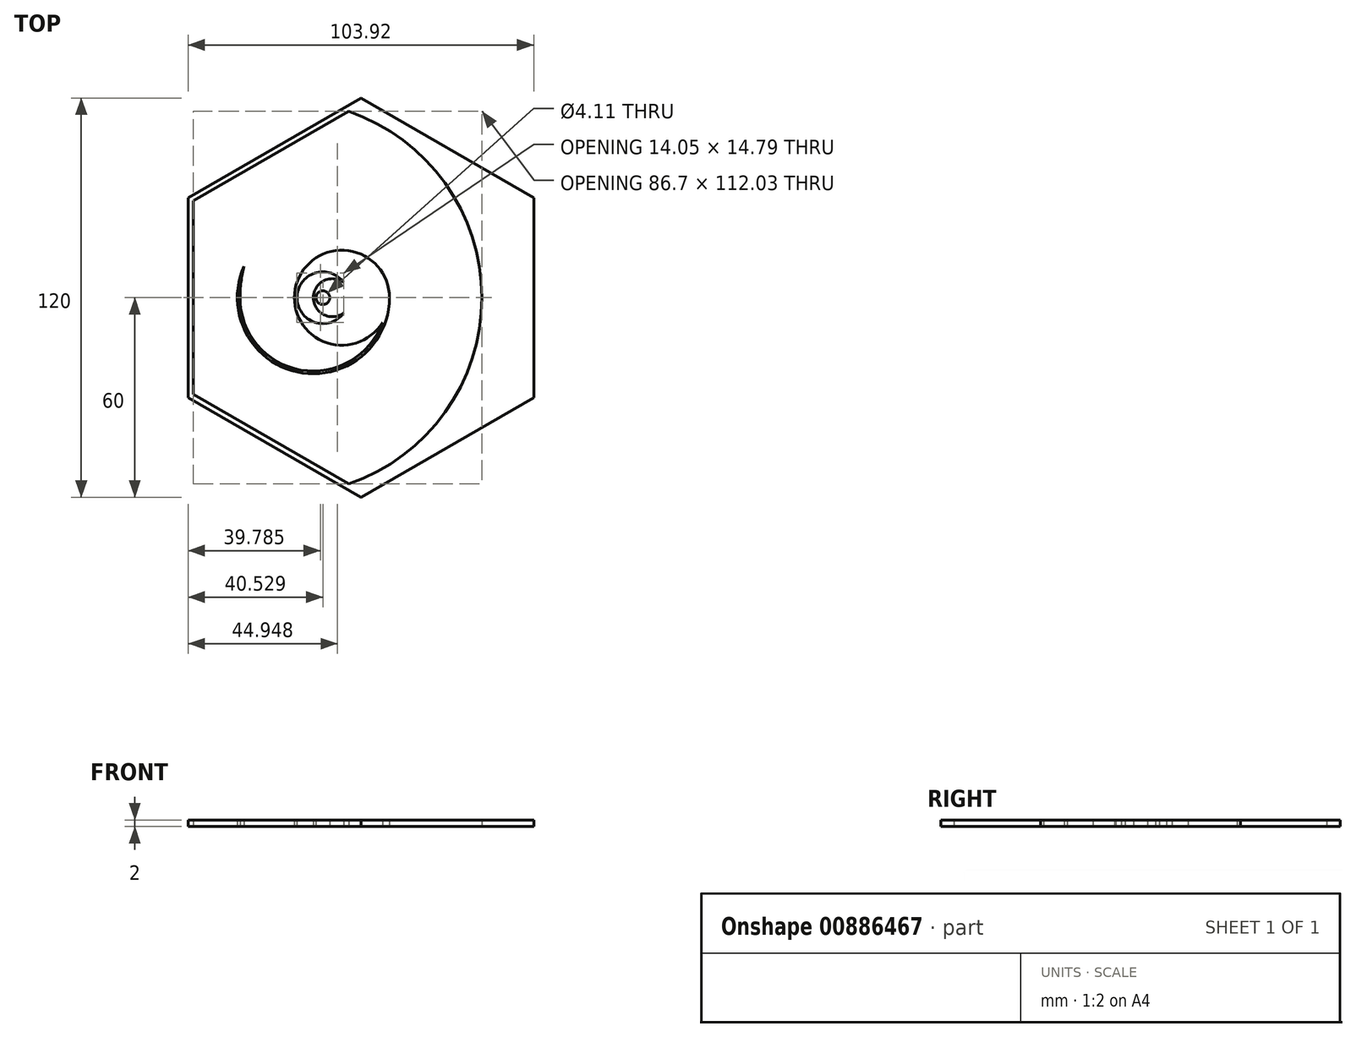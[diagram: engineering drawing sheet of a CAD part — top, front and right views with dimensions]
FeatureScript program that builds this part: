
annotation { "Feature Type Name" : "Feature", "Feature Type Description" : "" }
export const myFeature = defineFeature(function(context is Context, id is Id, definition is map)
    precondition{}
    {
        {
            var Q0;
            Q0=qCreatedBy(makeId("Top.planeOp"),FACE);
            var sketch = newSketch(context, id + "F0", { "sketchPlane" : qUnion([Q0])});
            skArc(sketch, "E0", {"start": v(41.43, 32.17) * mm, "mid": v(-14.29, 0) * mm, "end": v(41.43, -32.17) * mm});
            skCircle(sketch, "E1", {"center": v(8.57, 0) * mm, "radius": 22.86 * mm});
            skCircle(sketch, "E2", {"center": v(17.14, 0) * mm, "radius": 14.29 * mm});
            skCircle(sketch, "E3", {"center": v(11.43, 0) * mm, "radius": 8.57 * mm});
            skCircle(sketch, "E4", {"center": v(14.29, 0) * mm, "radius": 5.71 * mm});
            skArc(sketch, "E5.0", {"start": v(42.26, 30.73) * mm, "mid": v(-13.49, 0) * mm, "end": v(42.26, -30.73) * mm});
            skCircle(sketch, "E6.0", {"center": v(8.57, 0) * mm, "radius": 22.06 * mm});
            skCircle(sketch, "E7.0", {"center": v(17.14, 0) * mm, "radius": 13.49 * mm});
            skCircle(sketch, "E8.0", {"center": v(11.43, 0) * mm, "radius": 7.77 * mm});
            skCircle(sketch, "E9.0", {"center": v(14.29, 0) * mm, "radius": 4.91 * mm});
            skArc(sketch, "E10.trimOffspring", {"start": v(59.17, -1.43) * mm, "mid": v(59.2, 0) * mm, "end": v(59.17, 1.43) * mm});
            skCircle(sketch, "E11", {"center": v(22.86, 0) * mm, "radius": 36.34 * mm});
            skCircle(sketch, "E12", {"center": v(22.86, 0) * mm, "radius": 37.14 * mm});
            skCircle(sketch, "E13", {"center": v(11.43, 0) * mm, "radius": 2.86 * mm});
            skCircle(sketch, "E14.0", {"center": v(11.43, 0) * mm, "radius": 2.06 * mm});
            skCircle(sketch, "E15.cCircle", {"center": v(22.86, 0) * mm, "radius": 60 * mm, "construction": true});
            skLineSegment(sketch, "E15.0", {"start": v(-29.1, 30) * mm, "end": v(22.86, 60) * mm});
            skLineSegment(sketch, "E15.1", {"start": v(22.86, 60) * mm, "end": v(74.82, 30) * mm});
            skLineSegment(sketch, "E15.2", {"start": v(74.82, 30) * mm, "end": v(74.82, -30) * mm});
            skLineSegment(sketch, "E15.3", {"start": v(74.82, -30) * mm, "end": v(22.86, -60) * mm});
            skLineSegment(sketch, "E15.4", {"start": v(22.86, -60) * mm, "end": v(-29.1, -30) * mm});
            skLineSegment(sketch, "E15.5", {"start": v(-29.1, -30) * mm, "end": v(-29.1, 30) * mm});
            skArc(sketch, "E16", {"start": v(18.05, -57.22) * mm, "mid": v(60, 0) * mm, "end": v(18.05, 57.22) * mm});
            skArc(sketch, "E17.0", {"start": v(17.1, -56.68) * mm, "mid": v(59.2, 0) * mm, "end": v(17.1, 56.68) * mm});
            skLineSegment(sketch, "E18.0", {"start": v(-27.5, -29.08) * mm, "end": v(-27.5, 29.08) * mm});
            skLineSegment(sketch, "E18.1", {"start": v(22.86, 58.15) * mm, "end": v(73.22, 29.08) * mm});
            skLineSegment(sketch, "E18.2", {"start": v(73.22, 29.08) * mm, "end": v(73.22, -29.08) * mm});
            skLineSegment(sketch, "E18.3", {"start": v(-27.5, 29.08) * mm, "end": v(22.86, 58.15) * mm});
            skLineSegment(sketch, "E18.4", {"start": v(73.22, -29.08) * mm, "end": v(22.86, -58.15) * mm});
            skLineSegment(sketch, "E18.5", {"start": v(22.86, -58.15) * mm, "end": v(-27.5, -29.08) * mm});
            skPoint(sketch, "E19.orphan", {"position": v(-70.83, -30.73) * mm});
            skPoint(sketch, "E20.MirrorCS.start.orphan", {"position": v(-70.83, 30.73) * mm});
            skPoint(sketch, "E21.orphan", {"position": v(-70.03, -30.73) * mm});
            skPoint(sketch, "E22.orphan", {"position": v(-70.03, 30.73) * mm});
            skSolve(sketch);
        }
        {
            var Q0;
            {var subQ11=sQuery(id+"F0.wireOp",EDGE,"E15.1");Q0=makeQuery(id+"F0.imprint","IMPRINT",FACE,{"disambiguationData":[TD([[makeQuery(id+"F0.imprint","IMPRINT",EDGE,{"derivedFrom":subQ11}),-1.0]])]});}
            var Q1;
            {var subQ5=sQuery(id+"F0.wireOp",EDGE,"E15.5");Q1=makeQuery(id+"F0.imprint","IMPRINT",FACE,{"disambiguationData":[TD([[makeQuery(id+"F0.imprint","IMPRINT",EDGE,{"derivedFrom":subQ5}),-1.0]])]});}
            var Q2;
            {var subQ0=sQuery(id+"F0.wireOp",EDGE,"E16");var subQ1=sQuery(id+"F0.wireOp",EDGE,"E15.0");var subQ2=makeQuery(id+"F0.imprint","INTERSECT",VERTEX,{"derivedFrom":[subQ1,subQ0]});Q2=makeQuery(id+"F0.imprint","IMPRINT",FACE,{"disambiguationData":[TD([[makeQuery(id+"F0.imprint","IMPRINT",EDGE,{"disambiguationData":[TD([[subQ2,1.0]])],"derivedFrom":subQ1}),-1.0]])]});}
            var Q3;
            {var subQ0=sQuery(id+"F0.wireOp",EDGE,"E17.0");var subQ1=sQuery(id+"F0.wireOp",EDGE,"E12");var subQ2=makeQuery(id+"F0.imprint","INTERSECT",VERTEX,{"disambiguationData":[OD(0.0)],"derivedFrom":[subQ1,subQ0]});Q3=makeQuery(id+"F0.imprint","IMPRINT",FACE,{"disambiguationData":[TD([[makeQuery(id+"F0.imprint","IMPRINT",EDGE,{"disambiguationData":[TD([[subQ2,1.0]])],"derivedFrom":subQ1}),-1.0]])]});}
            var Q4;
            {var subQ6=sQuery(id+"F0.wireOp",EDGE,"E18.1");Q4=makeQuery(id+"F0.imprint","IMPRINT",FACE,{"disambiguationData":[TD([[makeQuery(id+"F0.imprint","IMPRINT",EDGE,{"derivedFrom":subQ6}),-1.0]])]});}
            var Q5;
            {var subQ0=sQuery(id+"F0.wireOp",EDGE,"E17.0");var subQ1=sQuery(id+"F0.wireOp",EDGE,"E12");var subQ2=makeQuery(id+"F0.imprint","INTERSECT",VERTEX,{"disambiguationData":[OD(0.0)],"derivedFrom":[subQ1,subQ0]});Q5=makeQuery(id+"F0.imprint","IMPRINT",FACE,{"disambiguationData":[TD([[makeQuery(id+"F0.imprint","IMPRINT",EDGE,{"disambiguationData":[TD([[subQ2,1.0]])],"derivedFrom":subQ1}),1.0]])]});}
            var Q6;
            {var subQ0=sQuery(id+"F0.wireOp",EDGE,"E11");var subQ1=makeQuery(id+"F0.imprint","IMPRINT",VERTEX,{"disambiguationData":[OD(0.0)],"derivedFrom":subQ0});Q6=makeQuery(id+"F0.imprint","IMPRINT",FACE,{"disambiguationData":[TD([[makeQuery(id+"F0.imprint","IMPRINT",EDGE,{"disambiguationData":[TD([[subQ1,-1.0]])],"derivedFrom":subQ0}),1.0]])]});}
            var Q7;
            {var subQ0=sQuery(id+"F0.wireOp",EDGE,"E11");var subQ9=makeQuery(id+"F0.imprint","IMPRINT",VERTEX,{"disambiguationData":[OD(0.0)],"derivedFrom":subQ0});Q7=makeQuery(id+"F0.imprint","IMPRINT",FACE,{"disambiguationData":[TD([[makeQuery(id+"F0.imprint","IMPRINT",EDGE,{"disambiguationData":[TD([[subQ9,-1.0]])],"derivedFrom":subQ0}),-1.0]])]});}
            var Q8;
            {var subQ0=sQuery(id+"F0.wireOp",EDGE,"E11");var subQ4=makeQuery(id+"F0.imprint","IMPRINT",VERTEX,{"disambiguationData":[OD(2.0)],"derivedFrom":subQ0});Q8=makeQuery(id+"F0.imprint","IMPRINT",FACE,{"disambiguationData":[TD([[makeQuery(id+"F0.imprint","IMPRINT",EDGE,{"disambiguationData":[TD([[subQ4,-1.0]])],"derivedFrom":subQ0}),-1.0]])]});}
            var Q9;
            {var subQ0=sQuery(id+"F0.wireOp",EDGE,"E16");var subQ1=sQuery(id+"F0.wireOp",EDGE,"E12");var subQ2=makeQuery(id+"F0.imprint","INTERSECT",VERTEX,{"derivedFrom":[subQ1,subQ0]});Q9=makeQuery(id+"F0.imprint","IMPRINT",FACE,{"disambiguationData":[TD([[makeQuery(id+"F0.imprint","IMPRINT",EDGE,{"disambiguationData":[TD([[subQ2,1.0]])],"derivedFrom":subQ1}),-1.0]])]});}
            var Q10;
            {var subQ0=sQuery(id+"F0.wireOp",EDGE,"E16");var subQ1=sQuery(id+"F0.wireOp",EDGE,"E15.4");var subQ2=makeQuery(id+"F0.imprint","INTERSECT",VERTEX,{"derivedFrom":[subQ1,subQ0]});Q10=makeQuery(id+"F0.imprint","IMPRINT",FACE,{"disambiguationData":[TD([[makeQuery(id+"F0.imprint","IMPRINT",EDGE,{"disambiguationData":[TD([[subQ2,-1.0]])],"derivedFrom":subQ1}),-1.0]])]});}
            var Q11;
            {var subQ0=sQuery(id+"F0.wireOp",EDGE,"E2");var subQ1=makeQuery(id+"F0.imprint","INTERSECT",VERTEX,{"derivedFrom":[sQuery(id+"F0.wireOp",EDGE,"E1"),subQ0]});Q11=makeQuery(id+"F0.imprint","IMPRINT",FACE,{"disambiguationData":[TD([[makeQuery(id+"F0.imprint","IMPRINT",EDGE,{"disambiguationData":[TD([[subQ1,-1.0]])],"derivedFrom":subQ0}),1.0]])]});}
            var Q12;
            {var subQ0=sQuery(id+"F0.wireOp",EDGE,"E2");var subQ1=sQuery(id+"F0.wireOp",EDGE,"E1");var subQ2=makeQuery(id+"F0.imprint","INTERSECT",VERTEX,{"derivedFrom":[subQ1,subQ0]});Q12=makeQuery(id+"F0.imprint","IMPRINT",FACE,{"disambiguationData":[TD([[makeQuery(id+"F0.imprint","IMPRINT",EDGE,{"disambiguationData":[TD([[subQ2,1.0]])],"derivedFrom":subQ1}),1.0]])]});}
            var Q13;
            {var subQ0=sQuery(id+"F0.wireOp",EDGE,"E11");var subQ1=sQuery(id+"F0.wireOp",EDGE,"E1");var subQ2=makeQuery(id+"F0.imprint","INTERSECT",VERTEX,{"disambiguationData":[OD(0.0)],"derivedFrom":[subQ1,subQ0]});Q13=makeQuery(id+"F0.imprint","IMPRINT",FACE,{"disambiguationData":[TD([[makeQuery(id+"F0.imprint","IMPRINT",EDGE,{"disambiguationData":[TD([[subQ2,1.0]])],"derivedFrom":subQ1}),1.0]])]});}
            var Q14;
            {var subQ0=sQuery(id+"F0.wireOp",EDGE,"E6.0");var subQ1=sQuery(id+"F0.wireOp",EDGE,"E2");var subQ2=makeQuery(id+"F0.imprint","INTERSECT",VERTEX,{"disambiguationData":[OD(0.0)],"derivedFrom":[subQ1,subQ0]});Q14=makeQuery(id+"F0.imprint","IMPRINT",FACE,{"disambiguationData":[TD([[makeQuery(id+"F0.imprint","IMPRINT",EDGE,{"disambiguationData":[TD([[subQ2,-1.0]])],"derivedFrom":subQ1}),1.0]])]});}
            var Q15;
            {var subQ0=sQuery(id+"F0.wireOp",EDGE,"E3");var subQ1=sQuery(id+"F0.wireOp",EDGE,"E2");var subQ2=makeQuery(id+"F0.imprint","INTERSECT",VERTEX,{"derivedFrom":[subQ1,subQ0]});Q15=makeQuery(id+"F0.imprint","IMPRINT",FACE,{"disambiguationData":[TD([[makeQuery(id+"F0.imprint","IMPRINT",EDGE,{"disambiguationData":[TD([[subQ2,-1.0]])],"derivedFrom":subQ1}),1.0]])]});}
            var Q16;
            {var subQ0=sQuery(id+"F0.wireOp",EDGE,"E4");var subQ1=makeQuery(id+"F0.imprint","INTERSECT",VERTEX,{"derivedFrom":[sQuery(id+"F0.wireOp",EDGE,"E3"),subQ0]});Q16=makeQuery(id+"F0.imprint","IMPRINT",FACE,{"disambiguationData":[TD([[makeQuery(id+"F0.imprint","IMPRINT",EDGE,{"disambiguationData":[TD([[subQ1,-1.0]])],"derivedFrom":subQ0}),1.0]])]});}
            var Q17;
            {var subQ0=sQuery(id+"F0.wireOp",EDGE,"E7.0");var subQ1=sQuery(id+"F0.wireOp",EDGE,"E3");var subQ2=makeQuery(id+"F0.imprint","INTERSECT",VERTEX,{"disambiguationData":[OD(0.0)],"derivedFrom":[subQ1,subQ0]});Q17=makeQuery(id+"F0.imprint","IMPRINT",FACE,{"disambiguationData":[TD([[makeQuery(id+"F0.imprint","IMPRINT",EDGE,{"disambiguationData":[TD([[subQ2,1.0]])],"derivedFrom":subQ1}),1.0]])]});}
            var Q18;
            {var subQ0=sQuery(id+"F0.wireOp",EDGE,"E4");var subQ1=sQuery(id+"F0.wireOp",EDGE,"E3");var subQ2=makeQuery(id+"F0.imprint","INTERSECT",VERTEX,{"derivedFrom":[subQ1,subQ0]});Q18=makeQuery(id+"F0.imprint","IMPRINT",FACE,{"disambiguationData":[TD([[makeQuery(id+"F0.imprint","IMPRINT",EDGE,{"disambiguationData":[TD([[subQ2,1.0]])],"derivedFrom":subQ1}),1.0]])]});}
            var Q19;
            {var subQ0=sQuery(id+"F0.wireOp",EDGE,"E13");var subQ1=sQuery(id+"F0.wireOp",EDGE,"E4");var subQ2=makeQuery(id+"F0.imprint","INTERSECT",VERTEX,{"derivedFrom":[subQ1,subQ0]});Q19=makeQuery(id+"F0.imprint","IMPRINT",FACE,{"disambiguationData":[TD([[makeQuery(id+"F0.imprint","IMPRINT",EDGE,{"disambiguationData":[TD([[subQ2,-1.0]])],"derivedFrom":subQ1}),1.0]])]});}
            var Q20;
            {var subQ0=sQuery(id+"F0.wireOp",EDGE,"E8.0");var subQ1=sQuery(id+"F0.wireOp",EDGE,"E4");var subQ2=makeQuery(id+"F0.imprint","INTERSECT",VERTEX,{"disambiguationData":[OD(0.0)],"derivedFrom":[subQ1,subQ0]});Q20=makeQuery(id+"F0.imprint","IMPRINT",FACE,{"disambiguationData":[TD([[makeQuery(id+"F0.imprint","IMPRINT",EDGE,{"disambiguationData":[TD([[subQ2,-1.0]])],"derivedFrom":subQ1}),1.0]])]});}
            var Q21;
            {var subQ0=sQuery(id+"F0.wireOp",EDGE,"E9.0");var subQ1=makeQuery(id+"F0.imprint","INTERSECT",VERTEX,{"derivedFrom":[subQ0,sQuery(id+"F0.wireOp",EDGE,"E14.0")]});Q21=makeQuery(id+"F0.imprint","IMPRINT",FACE,{"disambiguationData":[TD([[makeQuery(id+"F0.imprint","IMPRINT",EDGE,{"disambiguationData":[TD([[subQ1,1.0]])],"derivedFrom":subQ0}),-1.0]])]});}
            var Q22;
            {var subQ0=sQuery(id+"F0.wireOp",EDGE,"E3");var subQ1=makeQuery(id+"F0.imprint","INTERSECT",VERTEX,{"derivedFrom":[sQuery(id+"F0.wireOp",EDGE,"E2"),subQ0]});Q22=makeQuery(id+"F0.imprint","IMPRINT",FACE,{"disambiguationData":[TD([[makeQuery(id+"F0.imprint","IMPRINT",EDGE,{"disambiguationData":[TD([[subQ1,1.0]])],"derivedFrom":subQ0}),1.0]])]});}
            var Q23;
            {var subQ0=sQuery(id+"F0.wireOp",EDGE,"E7.0");var subQ1=sQuery(id+"F0.wireOp",EDGE,"E3");var subQ2=makeQuery(id+"F0.imprint","INTERSECT",VERTEX,{"disambiguationData":[OD(0.0)],"derivedFrom":[subQ1,subQ0]});Q23=makeQuery(id+"F0.imprint","IMPRINT",FACE,{"disambiguationData":[TD([[makeQuery(id+"F0.imprint","IMPRINT",EDGE,{"disambiguationData":[TD([[subQ2,1.0]])],"derivedFrom":subQ1}),-1.0]])]});}
            var Q24;
            {var subQ0=sQuery(id+"F0.wireOp",EDGE,"E9.0");var subQ1=makeQuery(id+"F0.imprint","INTERSECT",VERTEX,{"derivedFrom":[sQuery(id+"F0.wireOp",EDGE,"E8.0"),subQ0]});Q24=makeQuery(id+"F0.imprint","IMPRINT",FACE,{"disambiguationData":[TD([[makeQuery(id+"F0.imprint","IMPRINT",EDGE,{"disambiguationData":[TD([[subQ1,-1.0]])],"derivedFrom":subQ0}),1.0]])]});}
            var Q25;
            {var subQ0=sQuery(id+"F0.wireOp",EDGE,"E14.0");Q25=makeQuery(id+"F0.imprint","IMPRINT",FACE,{"disambiguationData":[TD([[makeQuery(id+"F0.imprint","IMPRINT",EDGE,{"derivedFrom":subQ0}),-1.0]])]});}
            var Q26;
            {var subQ0=sQuery(id+"F0.wireOp",EDGE,"E11");var subQ1=sQuery(id+"F0.wireOp",EDGE,"E1");var subQ2=makeQuery(id+"F0.imprint","INTERSECT",VERTEX,{"disambiguationData":[OD(0.0)],"derivedFrom":[subQ1,subQ0]});Q26=makeQuery(id+"F0.imprint","IMPRINT",FACE,{"disambiguationData":[TD([[makeQuery(id+"F0.imprint","IMPRINT",EDGE,{"disambiguationData":[TD([[subQ2,-1.0]])],"derivedFrom":subQ1}),1.0]])]});}
            var Q27;
            {var subQ0=sQuery(id+"F0.wireOp",EDGE,"a4ee45df-a419-48cb-ac47-d0f4e0d247c4.trimOffspring");var subQ1=sQuery(id+"F0.wireOp",EDGE,"E1");var subQ2=makeQuery(id+"F0.imprint","INTERSECT",VERTEX,{"disambiguationData":[OD(1.0)],"derivedFrom":[subQ1,subQ0]});Q27=makeQuery(id+"F0.imprint","IMPRINT",FACE,{"disambiguationData":[TD([[makeQuery(id+"F0.imprint","IMPRINT",EDGE,{"disambiguationData":[TD([[subQ2,-1.0]])],"derivedFrom":subQ1}),1.0]])]});}
            var Q28;
            {var subQ0=sQuery(id+"F0.wireOp",EDGE,"a4ee45df-a419-48cb-ac47-d0f4e0d247c4.trimOffspring");var subQ1=sQuery(id+"F0.wireOp",EDGE,"E1");var subQ2=makeQuery(id+"F0.imprint","INTERSECT",VERTEX,{"disambiguationData":[OD(0.0)],"derivedFrom":[subQ1,subQ0]});Q28=makeQuery(id+"F0.imprint","IMPRINT",FACE,{"disambiguationData":[TD([[makeQuery(id+"F0.imprint","IMPRINT",EDGE,{"disambiguationData":[TD([[subQ2,-1.0]])],"derivedFrom":subQ1}),1.0]])]});}
            var Q29;
            {var subQ0=sQuery(id+"F0.wireOp",EDGE,"a4ee45df-a419-48cb-ac47-d0f4e0d247c4.trimOffspring");var subQ1=sQuery(id+"F0.wireOp",EDGE,"E1");var subQ2=makeQuery(id+"F0.imprint","INTERSECT",VERTEX,{"disambiguationData":[OD(1.0)],"derivedFrom":[subQ1,subQ0]});Q29=makeQuery(id+"F0.imprint","IMPRINT",FACE,{"disambiguationData":[TD([[makeQuery(id+"F0.imprint","IMPRINT",EDGE,{"disambiguationData":[TD([[subQ2,-1.0]])],"derivedFrom":subQ0}),-1.0]])]});}
            var Q30;
            {var subQ0=sQuery(id+"F0.wireOp",EDGE,"a4ee45df-a419-48cb-ac47-d0f4e0d247c4.trimOffspring");var subQ1=sQuery(id+"F0.wireOp",EDGE,"E1");var subQ2=makeQuery(id+"F0.imprint","INTERSECT",VERTEX,{"disambiguationData":[OD(0.0)],"derivedFrom":[subQ1,subQ0]});Q30=makeQuery(id+"F0.imprint","IMPRINT",FACE,{"disambiguationData":[TD([[makeQuery(id+"F0.imprint","IMPRINT",EDGE,{"disambiguationData":[TD([[subQ2,1.0]])],"derivedFrom":subQ0}),-1.0]])]});}
            extrude(context, id + "F1", {"entities" : qUnion([Q0, Q1, Q2, Q3, Q4, Q5, Q6, Q7, Q8, Q9, Q10, Q11, Q12, Q13, Q14, Q15, Q16, Q17, Q18, Q19, Q20, Q21, Q22, Q23, Q24, Q25, Q26, Q27, Q28, Q29, Q30]), "depth" : 2 * mm, "offsetDistance" : 25 * mm});
        }
    });
